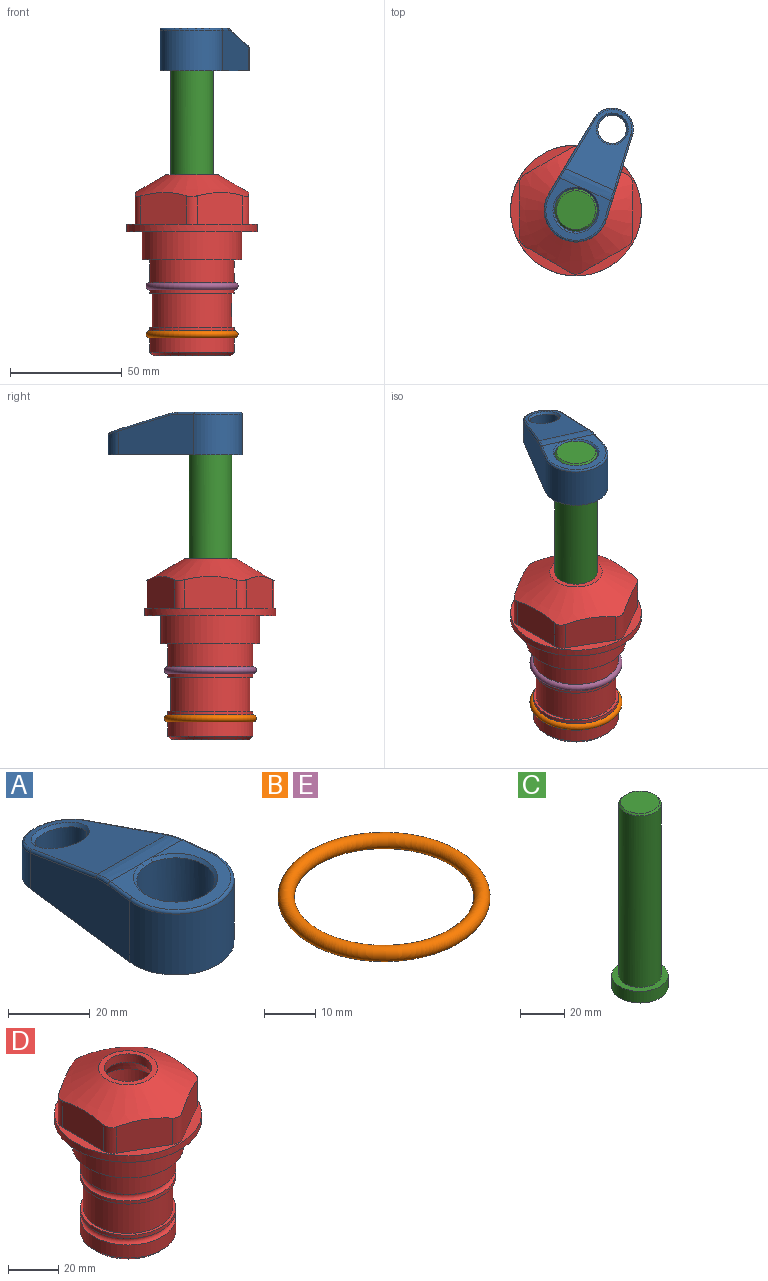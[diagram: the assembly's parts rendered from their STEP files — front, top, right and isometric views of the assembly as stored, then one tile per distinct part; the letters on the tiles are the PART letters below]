
ASSEMBLY  parts=5 mates=4
PART A: 31 faces, bbox 31.7x65.5x19.8 mm
  f0: plane 39.12x18.26mm, normal (0.99,0.12,0), area 612.2mm2, adj f1,f4,f7,f11,f13,f15
  f1: cylinder r=9.53mm len=18.91mm, axis (0,0,-1), area 296.1mm2, adj f0,f2,f7,f17
  f2: plane 39.12x18.26mm, normal (-0.99,0.12,0), area 612.2mm2, adj f1,f4,f7,f12,f14,f16
  f3: cylinder r=6.35mm len=12.7mm, axis (0,0,-1), area 362.4mm2, adj f7,f18
  f4: cylinder r=14.29mm len=28.58mm, axis (0,0,-1), area 882.2mm2, adj f0,f2,f7,f10
  f5: cylinder r=9.53mm len=19.05mm, axis (0,0,-1), area 1092.6mm2, adj f7,f19,f20
  f6: plane 26.99x23.69mm, normal (0,0,1), area 216.2mm2, adj f9,f10,f11,f12,f19
  f7: plane 63.5x28.58mm, normal (0,0,-1), area 661.8mm2, adj f0,f1,f2,f3,f4,f5,f22,f23
  f8: plane 33.52x23.6mm, normal (0,0.26,0.97), area 486mm2, adj f9,f15,f16,f17,f18
  f9: cylinder r=19.05mm len=24.72mm, axis (1,0,0), area 120.4mm2, adj f6,f8,f13,f14,f20
  f10: torus R=13.49mm, axis (0,0,1), area 59mm2, adj f4,f6,f11,f12
  f11: cylinder r=0.79mm len=8.67mm, axis (0.12,-0.99,0), area 10.8mm2, adj f0,f6,f10,f13
  f12: cylinder r=0.79mm len=8.67mm, axis (0.12,0.99,0), area 10.8mm2, adj f2,f6,f10,f14
  f13: bspline ~4.95x1.42mm, area 6.1mm2, adj f0,f9,f11,f15
  f14: bspline ~4.95x1.42mm, area 6.1mm2, adj f2,f9,f12,f16
  f15: cylinder r=0.79mm len=25.95mm, axis (0.12,-0.96,0.26), area 32.9mm2, adj f0,f8,f13,f17
  f16: cylinder r=0.79mm len=25.95mm, axis (0.12,0.96,-0.26), area 32.9mm2, adj f2,f8,f14,f17
  f17: bspline ~18.91x8.38mm, area 30mm2, adj f1,f8,f15,f16
  f18: bspline ~14.29x14.29mm, area 48.3mm2, adj f3,f8
  f19: cone r=9.53mm half-angle=45deg, axis (0,0,1), area 66.5mm2, adj f5,f6,f20
  f20: bspline ~3.22x0.96mm, area 3.5mm2, adj f5,f9,f19
  f21: plane 2.75x2.72mm, normal (0,0,-1), area 2.9mm2, adj f23,f25,f28
  f22: plane 23.05x15.88mm, normal (-0.99,-0.12,0), area 323.6mm2, adj f7,f25,f26,f27,f28,f29
  f23: plane 23.05x15.88mm, normal (0.99,-0.12,0), area 323.6mm2, adj f7,f21,f25,f27,f28,f30
  f24: cylinder r=9.53mm len=10.69mm, axis (0,0,-1), area 114.7mm2, adj f7,f27,f29,f30
  f25: cylinder r=12.7mm len=20.59mm, axis (0,0,-1), area 381.1mm2, adj f7,f21,f22,f23,f26,f28
  f26: plane 2.75x2.72mm, normal (0,0,-1), area 2.9mm2, adj f22,f25,f28
  f27: plane 19.72x18.37mm, normal (0,-0.26,-0.97), area 291.8mm2, adj f22,f23,f24,f28,f29,f30
  f28: cylinder r=15.88mm len=19.92mm, axis (1,0,0), area 54.8mm2, adj f21,f22,f23,f25,f26,f27
  f29: cylinder r=1.59mm len=11mm, axis (0,0,-1), area 34.7mm2, adj f7,f22,f24,f27
  f30: cylinder r=1.59mm len=11mm, axis (0,0,-1), area 34.7mm2, adj f7,f23,f24,f27
PART B: 1 faces, bbox 44.7x44.7x3.2 mm
  f0: torus R=19.05mm, axis (0,0,1), area 1193.9mm2
PART C: 6 faces, bbox 25.4x25.4x101.6 mm
  f0: plane 17.46x17.46mm, normal (0,0,1), area 239.5mm2, adj f5
  f1: plane 25.4x25.4mm, normal (0,0,-1), area 506.7mm2, adj f2
  f2: cylinder r=12.7mm len=25.4mm, axis (0,0,1), area 506.7mm2, adj f1,f3
  f3: plane 25.4x25.4mm, normal (0,0,1), area 221.7mm2, adj f2,f4
  f4: cylinder r=9.53mm len=94.46mm, axis (0,0,1), area 5653mm2, adj f3,f5
  f5: cone r=8.73mm half-angle=45deg, axis (0,0,-1), area 64.4mm2, adj f0,f4
PART D: 36 faces, bbox 58.7x58.7x81 mm
  f0: cylinder r=17.78mm len=35.56mm, axis (0,0,1), area 1670.8mm2, adj f23,f24,f31
  f1: cylinder r=19.05mm len=38.1mm, axis (0,0,1), area 1191.9mm2, adj f26,f27,f30
  f2: plane 58.66x58.66mm, normal (0,0,-1), area 1150.6mm2, adj f3,f28
  f3: cylinder r=29.33mm len=58.66mm, axis (0,0,-1), area 585.1mm2, adj f2,f4
  f4: plane 58.66x58.66mm, normal (0,0,1), area 475.9mm2, adj f3,f5,f6,f7,f8,f9,f10,f11
  f5: plane 20.32x14.34mm, normal (-0.5,0.87,0), area 324.4mm2, adj f4,f15,f16,f17
  f6: plane 20.32x14.34mm, normal (0.5,0.87,0), area 324.4mm2, adj f4,f14,f15,f17
  f7: plane 23.48x14.34mm, normal (1,0,0), area 324.4mm2, adj f4,f13,f14,f17
  f8: plane 20.32x14.34mm, normal (0.5,-0.87,0), area 324.4mm2, adj f4,f12,f13,f17
  f9: plane 20.32x14.34mm, normal (-0.5,-0.87,0), area 324.4mm2, adj f4,f11,f12,f17
  f10: plane 23.48x14.34mm, normal (-1,0,0), area 324.4mm2, adj f4,f11,f16,f17
  f11: cylinder r=5.08mm len=12.85mm, axis (0,0,-1), area 67.2mm2, adj f4,f9,f10,f17
  f12: cylinder r=5.08mm len=12.85mm, axis (0,0,-1), area 67.2mm2, adj f4,f8,f9,f17
  f13: cylinder r=5.08mm len=12.85mm, axis (0,0,-1), area 67.2mm2, adj f4,f7,f8,f17
  f14: cylinder r=5.08mm len=12.85mm, axis (0,0,-1), area 67.2mm2, adj f4,f6,f7,f17
  f15: cylinder r=5.08mm len=12.85mm, axis (0,0,-1), area 67.2mm2, adj f4,f5,f6,f17
  f16: cylinder r=5.08mm len=12.85mm, axis (0,0,-1), area 67.2mm2, adj f4,f5,f10,f17
  f17: cone r=11.73mm half-angle=60deg, axis (0,0,-1), area 2071.8mm2, adj f5,f6,f7,f8,f9,f10,f11,f12
  f18: plane 23.46x23.46mm, normal (0,0,1), area 147.4mm2, adj f17,f35
  f19: plane 34.93x34.93mm, normal (0,0,-1), area 958mm2, adj f29
  f20: cylinder r=19.05mm len=38.1mm, axis (0,0,1), area 760.1mm2, adj f21,f29
  f21: torus R=19.05mm, axis (0,0,1), area 565.3mm2, adj f20,f22
  f22: cylinder r=19.05mm len=38.1mm, axis (0,0,1), area 190mm2, adj f21,f23
  f23: plane 38.1x38.1mm, normal (0,0,1), area 146.9mm2, adj f0,f22
  f24: plane 38.1x38.1mm, normal (0,0,-1), area 146.9mm2, adj f0,f25
  f25: cylinder r=19.05mm len=38.1mm, axis (0,0,1), area 190mm2, adj f24,f26
  f26: torus R=19.05mm, axis (0,0,1), area 565.3mm2, adj f1,f25
  f27: plane 44.45x44.45mm, normal (0,0,-1), area 411.7mm2, adj f1,f28
  f28: cylinder r=22.23mm len=44.45mm, axis (0,0,1), area 1773.5mm2, adj f2,f27
  f29: cone r=19.05mm half-angle=45deg, axis (0,0,1), area 257.5mm2, adj f19,f20
  f30: cylinder r=3.17mm len=6.75mm, axis (-1,0,0), area 128mm2, adj f1,f33
  f31: cylinder r=3.17mm len=6.35mm, axis (-1,0,0), area 102.5mm2, adj f0,f33
  f32: plane 25.4x25.4mm, normal (0,0,1), area 506.7mm2, adj f33
  f33: cylinder r=12.7mm len=66.42mm, axis (0,0,-1), area 5236.2mm2, adj f30,f31,f32,f34
  f34: cone r=9.53mm half-angle=30deg, axis (0,0,-1), area 443.4mm2, adj f33,f35
  f35: cylinder r=9.53mm len=19.05mm, axis (0,0,-1), area 240.9mm2, adj f18,f34
PART E: same geometry as B
PLACE A rot(axis=(0,0,-1),24.1deg) t=(0,0,27.55)mm
PLACE B t=(0,0,-21.59)mm
PLACE C rot(axis=(0,0,-1),24.1deg) t=(0,0,27.55)mm
PLACE D at identity fixed
PLACE E at identity
MATE fastened B.f0 <-> D.f0  axis (0,0,1) through (0,0,-46.1)mm
MATE cylindrical C.f2 <-> D.f0  axis (0,0,-1) through (0,0,-10.55)mm
MATE fastened A.f4 <-> C.f2  axis (0,0,1) through (0,0,91.05)mm
MATE fastened E.f0 <-> D.f0  axis (0,0,1) through (0,0,-24.51)mm
